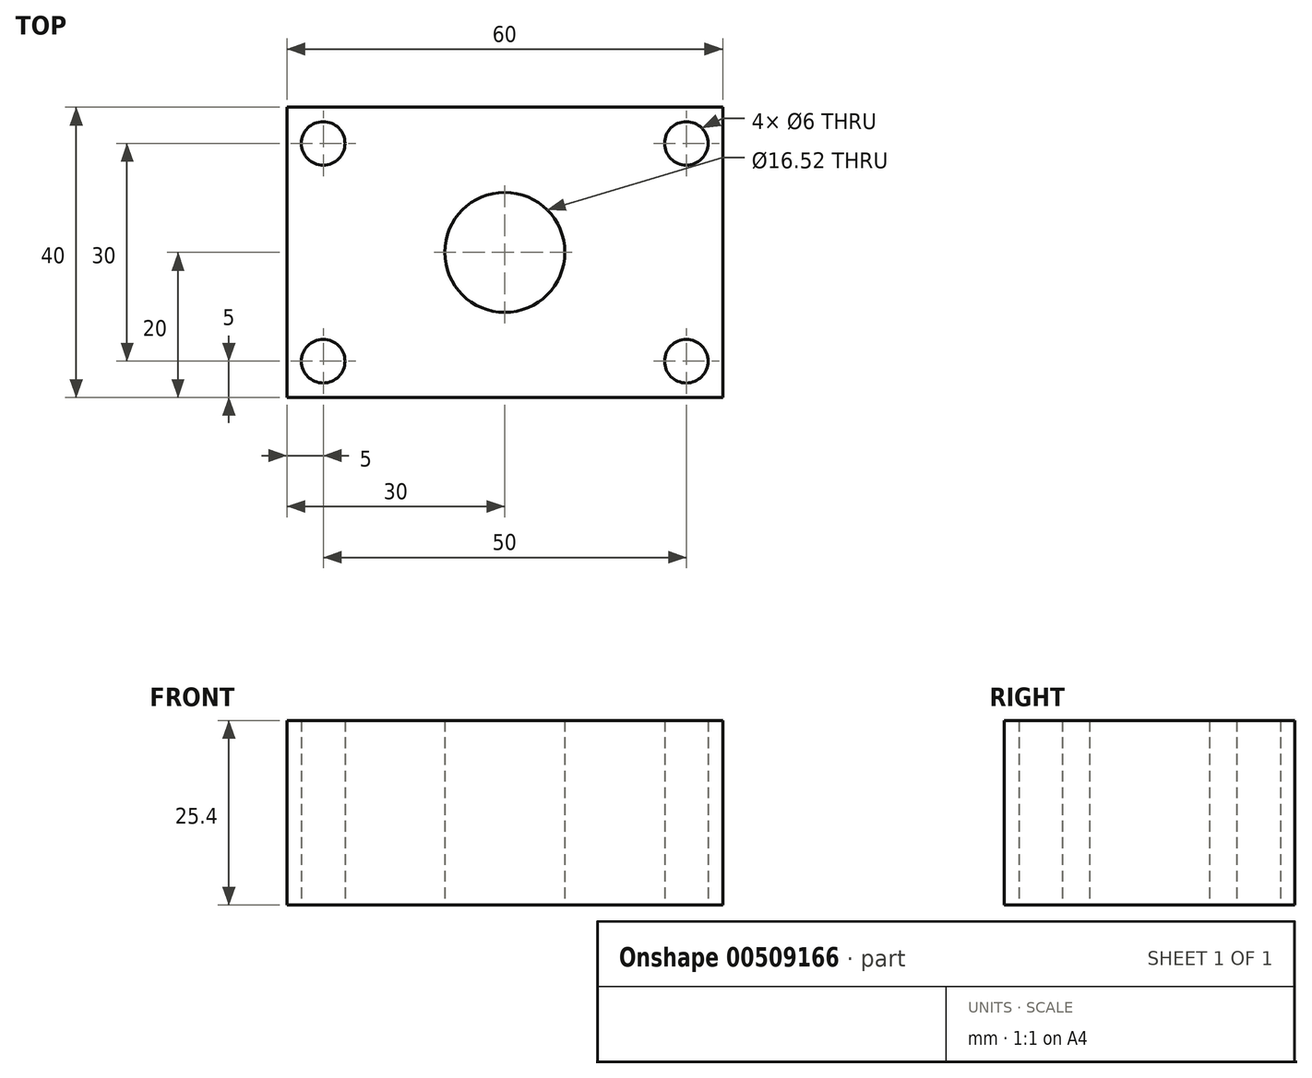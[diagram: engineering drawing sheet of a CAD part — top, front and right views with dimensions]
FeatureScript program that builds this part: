
annotation { "Feature Type Name" : "Feature", "Feature Type Description" : "" }
export const myFeature = defineFeature(function(context is Context, id is Id, definition is map)
    precondition{}
    {
        {
            var Q0;
            Q0=qCreatedBy(makeId("Top.planeOp"),FACE);
            var sketch = newSketch(context, id + "F0", { "sketchPlane" : qUnion([Q0])});
            skLineSegment(sketch, "E0.bottom", {"start": v(30, 20) * mm, "end": v(-30, 20) * mm});
            skLineSegment(sketch, "E0.top", {"start": v(30, -20) * mm, "end": v(-30, -20) * mm});
            skLineSegment(sketch, "E0.left", {"start": v(30, 20) * mm, "end": v(30, -20) * mm});
            skLineSegment(sketch, "E0.right", {"start": v(-30, 20) * mm, "end": v(-30, -20) * mm});
            skPoint(sketch, "E0.middle", {"position": v(0, 0) * mm});
            skLineSegment(sketch, "E1.bottom", {"start": v(25, 15) * mm, "end": v(-25, 15) * mm});
            skLineSegment(sketch, "E1.top", {"start": v(25, -15) * mm, "end": v(-25, -15) * mm});
            skLineSegment(sketch, "E1.left", {"start": v(25, 15) * mm, "end": v(25, -15) * mm});
            skLineSegment(sketch, "E1.right", {"start": v(-25, 15) * mm, "end": v(-25, -15) * mm});
            skCircle(sketch, "E2", {"center": v(-25, 15) * mm, "radius": 3 * mm});
            skCircle(sketch, "E3", {"center": v(-25, -15) * mm, "radius": 3 * mm});
            skCircle(sketch, "E4", {"center": v(25, -15) * mm, "radius": 3 * mm});
            skCircle(sketch, "E5", {"center": v(25, 15) * mm, "radius": 3 * mm});
            skCircle(sketch, "E6", {"center": v(0, 0) * mm, "radius": 8.26 * mm});
            skSolve(sketch);
        }
        {
            var Q0;
            Q0=qCreatedBy(makeId("Top.planeOp"),FACE);
            var sketch = newSketch(context, id + "F1", { "sketchPlane" : qUnion([Q0])});
            skSolve(sketch);
        }
        {
            var Q0;
            Q0 = qSketchRegion(id + "F1", true);
            var Q1;
            Q1=makeQuery(id+"F0.imprint","IMPRINT",FACE,{"disambiguationData":[TD([[makeQuery(id+"F0.imprint","IMPRINT",EDGE,{"derivedFrom":sQuery(id+"F0.wireOp",EDGE,"E0.bottom")}),1.0]])]});
            var Q2;
            Q2=makeQuery(id+"F0.imprint","IMPRINT",FACE,{"disambiguationData":[TD([[makeQuery(id+"F0.imprint","IMPRINT",EDGE,{"derivedFrom":sQuery(id+"F0.wireOp",EDGE,"E6")}),-1.0]])]});
            extrude(context, id + "F2", {"entities" : qUnion([Q0, Q1, Q2]), "depth" : 25.4 * mm});
        }
    });
